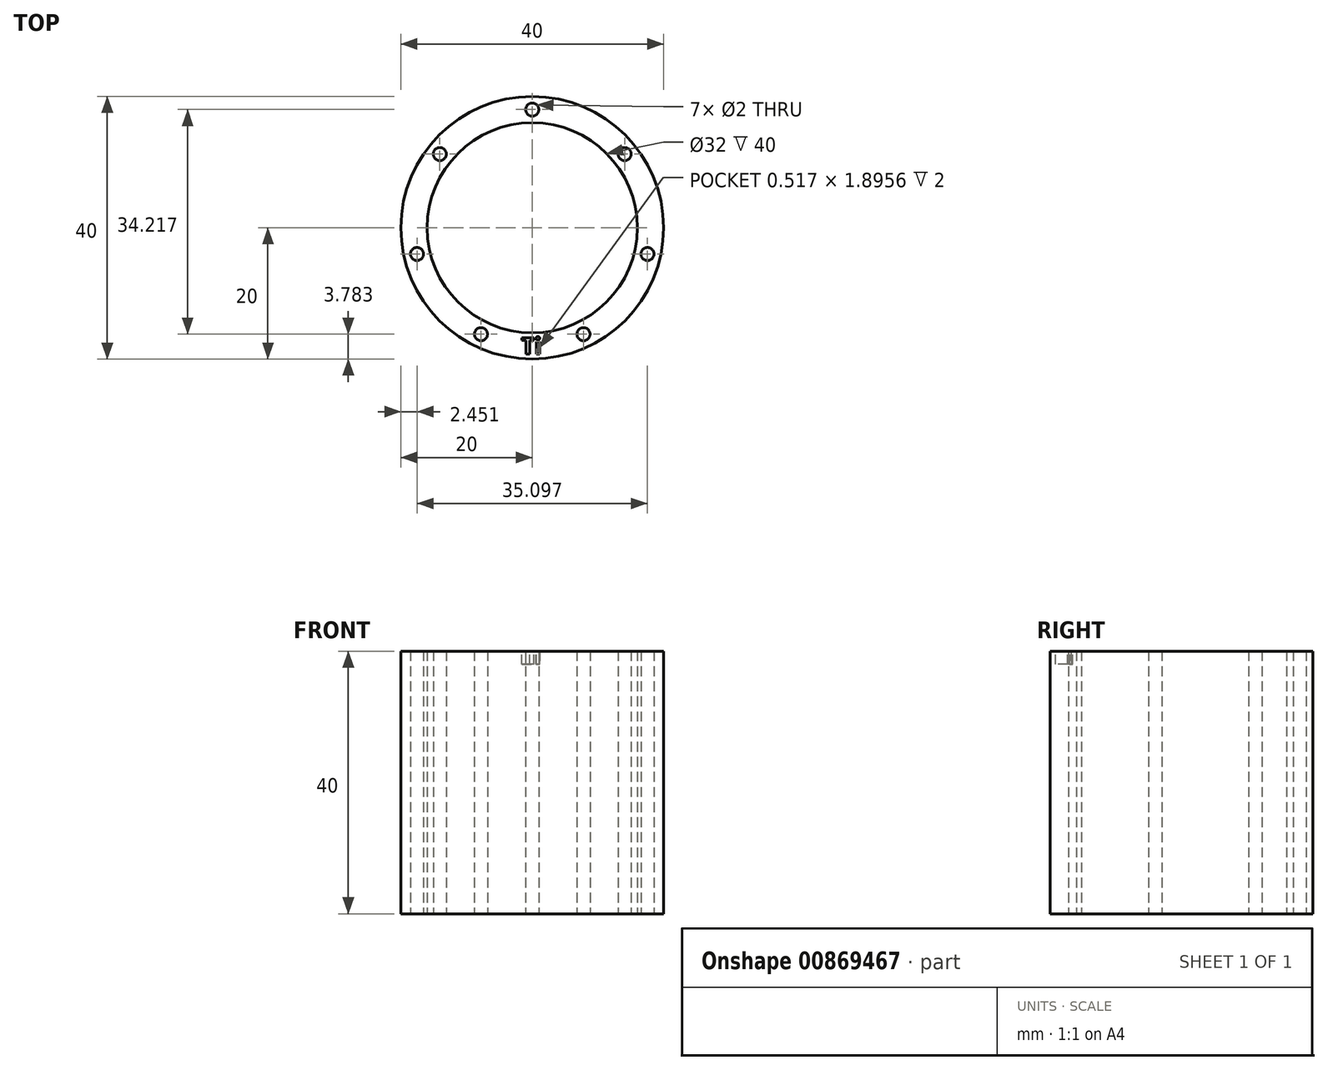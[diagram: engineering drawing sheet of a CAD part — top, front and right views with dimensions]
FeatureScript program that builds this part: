
annotation { "Feature Type Name" : "Feature", "Feature Type Description" : "" }
export const myFeature = defineFeature(function(context is Context, id is Id, definition is map)
    precondition{}
    {
        {
            var Q0;
            Q0=qCreatedBy(makeId("Top.planeOp"),FACE);
            var sketch = newSketch(context, id + "F0", { "sketchPlane" : qUnion([Q0])});
            skCircle(sketch, "E0", {"center": v(0, 0) * mm, "radius": 16 * mm});
            skCircle(sketch, "E1", {"center": v(0, 0) * mm, "radius": 20 * mm});
            skCircle(sketch, "E2", {"center": v(0, 18) * mm, "radius": 1 * mm});
            skCircle(sketch, "E3.1.0", {"center": v(-14.07, 11.22) * mm, "radius": 1 * mm});
            skCircle(sketch, "E3.2.0", {"center": v(-17.55, -4) * mm, "radius": 1 * mm});
            skCircle(sketch, "E3.3.0", {"center": v(-7.8, -16.22) * mm, "radius": 1 * mm});
            skCircle(sketch, "E3.4.0", {"center": v(7.8, -16.22) * mm, "radius": 1 * mm});
            skCircle(sketch, "E3.5.0", {"center": v(17.55, -4) * mm, "radius": 1 * mm});
            skCircle(sketch, "E3.6.0", {"center": v(14.07, 11.22) * mm, "radius": 1 * mm});
            skSolve(sketch);
        }
        {
            var Q0;
            Q0=makeQuery(id+"F0.imprint","IMPRINT",FACE,{"disambiguationData":[TD([[makeQuery(id+"F0.imprint","IMPRINT",EDGE,{"derivedFrom":sQuery(id+"F0.wireOp",EDGE,"E0")}),-1.0]])]});
            extrude(context, id + "F1", {"entities" : qUnion([Q0]), "depth" : 40 * mm, "offsetDistance" : 25 * mm});
        }
        {
            var Q0;
            Q0=makeQuery(id+"F1.opExtrude","CAP_FACE",FACE,{"disambiguationData":[OSD([sQuery(id+"F0.wireOp",EDGE,"E0"),sQuery(id+"F0.wireOp",EDGE,"E1"),sQuery(id+"F0.wireOp",EDGE,"E2"),sQuery(id+"F0.wireOp",EDGE,"E3.1.0"),sQuery(id+"F0.wireOp",EDGE,"E3.2.0"),sQuery(id+"F0.wireOp",EDGE,"E3.3.0"),sQuery(id+"F0.wireOp",EDGE,"E3.4.0"),sQuery(id+"F0.wireOp",EDGE,"E3.5.0"),sQuery(id+"F0.wireOp",EDGE,"E3.6.0")])],"isStart":false});
            var sketch = newSketch(context, id + "F2", { "sketchPlane" : qUnion([Q0])});
            skText(sketch, "E4", { "text": "Ti", "fontName": "OpenSans-Bold.ttf"});
            const initialGuessF2  = {"E4": [-0.00168, -0.01922, 1, 0, 0.0025]};
            skSetInitialGuess(sketch, initialGuessF2);
            skSolve(sketch);
        }
        {
            var Q0;
            Q0 = qSketchRegion(id + "F2", true);
            extrude(context, id + "F3", {"entities" : qUnion([Q0]), "operationType" : NewBodyOperationType.REMOVE, "oppositeDirection" : true, "depth" : 2 * mm, "offsetDistance" : 25 * mm});
        }
    });
